# Revit family: DoorOpener_Garage_Liftmaster_Residential-13Series
name_source: partatom
category: Specialty Equipment
revit_build: Autodesk Revit 2016 (Build: 20150714_1515(x64)
units: mm (PartAtom-declared; Revit-internal decimal feet)

## family parameters
Always vertical = Yes
Cut with Voids When Loaded = No
Part Type = Normal
Room Calculation Point = No
Round Connector Dimension = Use Diameter
Shared = No
Work Plane-Based = Yes

## types (2) — shared parameters
Accent Material = Plastic - Liftmaster - White
Assembly Code = E1030900
Construction Details = http://www.arcat.com
Default Elevation = 4' - 0"
Drive Type = Chain Drive
Green Building-LEED = http://www.arcat.com
Installation-Fabrication = http://www.liftmaster.com
Keynote = 08730
Light Compartment Depth = 0' - 4 1/2"
Manufacturer = LiftMaster - The Chamberlain Group, Inc.
Manufacturer Fax = 877-361-9589
Manufacturer Website = http://www.liftmaster.com
Material = Plastic - Liftmaster - Black
Max Door Height = 10' - 0"
Product Data = http://www.arcat.com
Revision = R1_07-2011
Sales Information = http://www.liftmaster.com
Send Message = http://www.arcat.com
Specification = http://www.arcat.com
Support Material = Metal - Steel - Liftmaster - Powder Coat - Black
Track Material = Metal - Aluminum - Liftmaster - Anodized - Clear
URL = http://www.liftmaster.com
Unit Depth = 2' - 0"
Unit Height = 0' - 11"
Unit Width = 1' - 4"
zero-valued in all types: Expected Lifespan (Years), Maintenance Schedule (Months), Warranty Duration (Years)

## per-type parameters (varying)
| type | Description | Motor HP |
| 1355/1356 | Liftmaster Chain Drive Residential Garage Door Opertator - Model 1355/1356 | 0.5 |
| 1345/1346 | Liftmaster Chain Drive Residential Garage Door Opertator - Model 1345/1346 | 0.666667 |

note: column(s) folded — value = type name in every type: Model

## geometry (parser evidence)
native form markers: Blend x12, Sweep x6
no freeform markers — native parametric forms only
